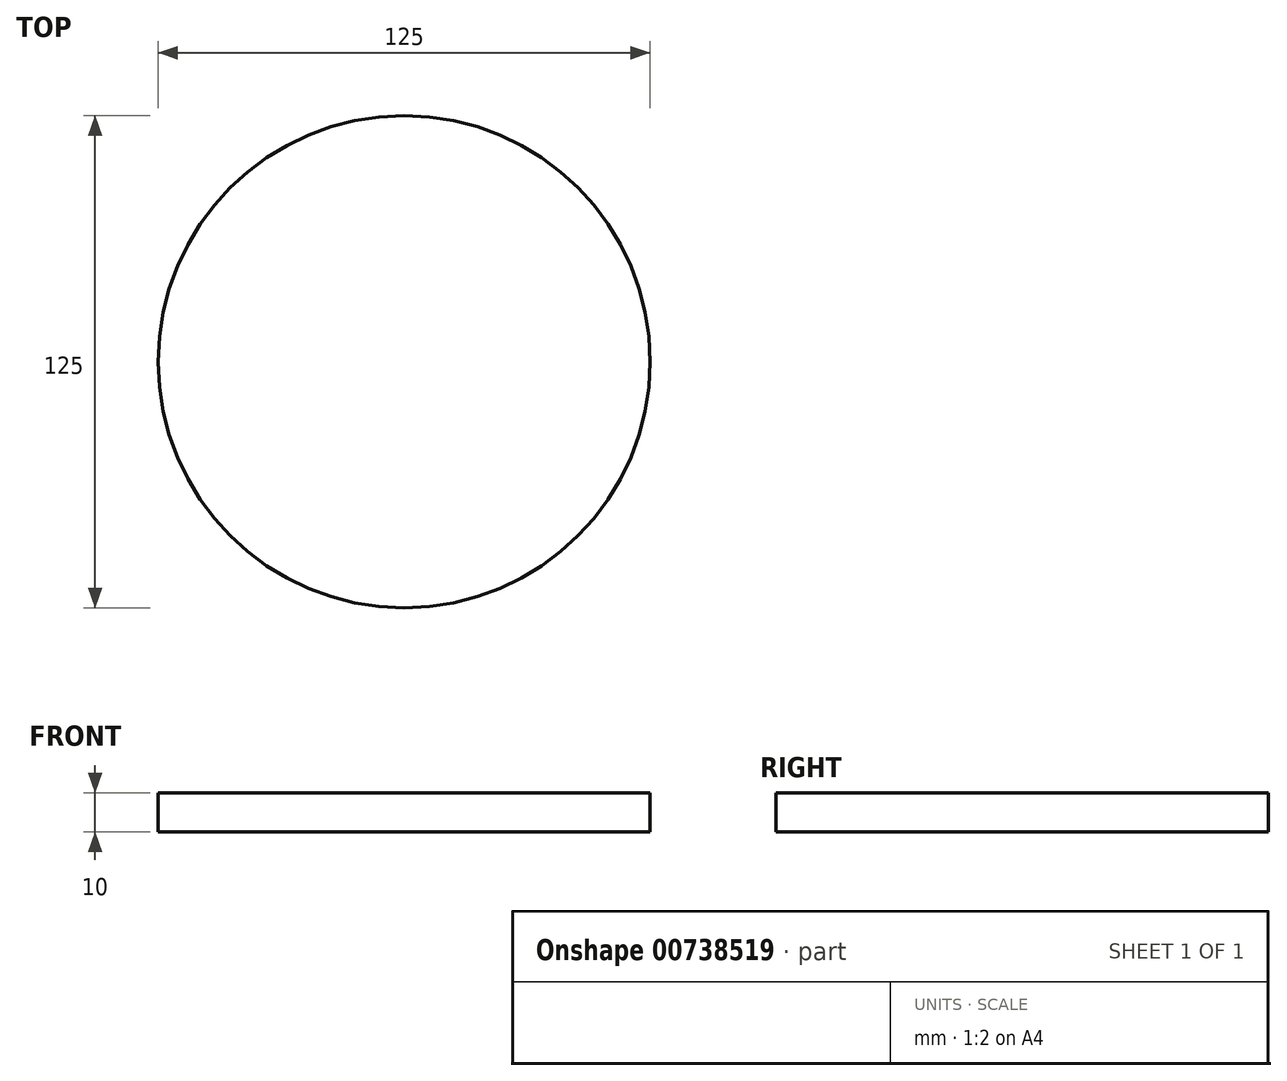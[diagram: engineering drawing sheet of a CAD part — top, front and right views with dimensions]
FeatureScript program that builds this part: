
annotation { "Feature Type Name" : "Feature", "Feature Type Description" : "" }
export const myFeature = defineFeature(function(context is Context, id is Id, definition is map)
    precondition{}
    {
        {
            var Q0;
            Q0=qCreatedBy(makeId("Top.planeOp"),FACE);
            var sketch = newSketch(context, id + "F0", { "sketchPlane" : qUnion([Q0])});
            skCircle(sketch, "E0", {"center": v(0, 0) * mm, "radius": 62.5 * mm});
            skSolve(sketch);
        }
        {
            var Q0;
            Q0=makeQuery(id+"F0.imprint","IMPRINT",FACE,{"disambiguationData":[TD([[makeQuery(id+"F0.imprint","IMPRINT",EDGE,{"derivedFrom":sQuery(id+"F0.wireOp",EDGE,"E0")}),1.0]])]});
            extrude(context, id + "F1", {"entities" : qUnion([Q0]), "depth" : 10 * mm, "offsetDistance" : 25 * mm});
        }
    });
